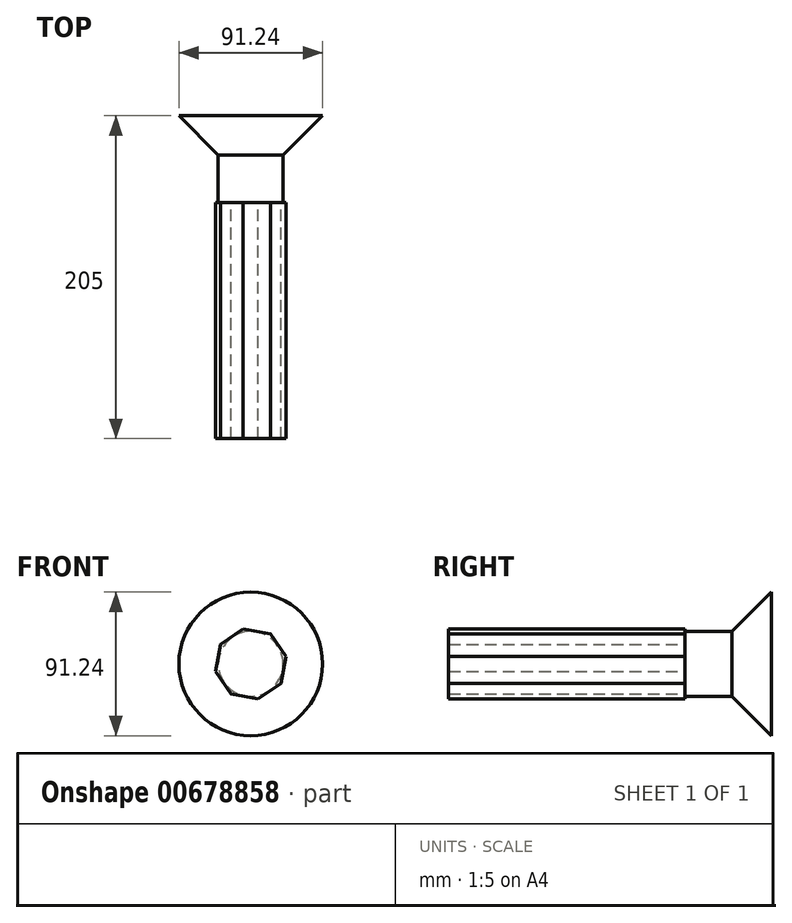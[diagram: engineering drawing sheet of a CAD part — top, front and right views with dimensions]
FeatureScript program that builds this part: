
annotation { "Feature Type Name" : "Feature", "Feature Type Description" : "" }
export const myFeature = defineFeature(function(context is Context, id is Id, definition is map)
    precondition{}
    {
        {
            var Q0;
            Q0=qCreatedBy(makeId("Front.planeOp"),FACE);
            var sketch = newSketch(context, id + "F0", { "sketchPlane" : qUnion([Q0])});
            skLineSegment(sketch, "E0.0", {"start": v(19.13, -12.45) * mm, "end": v(4.73, -22.33) * mm});
            skLineSegment(sketch, "E0.1", {"start": v(4.73, -22.33) * mm, "end": v(-12.45, -19.13) * mm});
            skLineSegment(sketch, "E0.2", {"start": v(-12.45, -19.13) * mm, "end": v(-22.33, -4.73) * mm});
            skLineSegment(sketch, "E0.3", {"start": v(-22.33, -4.73) * mm, "end": v(-19.13, 12.45) * mm});
            skLineSegment(sketch, "E0.4", {"start": v(-19.13, 12.45) * mm, "end": v(-4.73, 22.33) * mm});
            skLineSegment(sketch, "E0.5", {"start": v(-4.73, 22.33) * mm, "end": v(12.45, 19.13) * mm});
            skLineSegment(sketch, "E0.6", {"start": v(12.45, 19.13) * mm, "end": v(22.33, 4.73) * mm});
            skLineSegment(sketch, "E0.7", {"start": v(22.33, 4.73) * mm, "end": v(19.13, -12.45) * mm});
            skSolve(sketch);
        }
        {
            var Q0;
            Q0=makeQuery(id+"F0.imprint","IMPRINT",FACE,{"disambiguationData":[TD([[makeQuery(id+"F0.imprint","IMPRINT",EDGE,{"derivedFrom":sQuery(id+"F0.wireOp",EDGE,"E0.0")}),-1.0]])]});
            var Q1;
            Q1=sQuery(id+"F0.wireOp",EDGE,"E0.0");
            var Q2;
            Q2=sQuery(id+"F0.wireOp",EDGE,"E0.1");
            var Q3;
            Q3=sQuery(id+"F0.wireOp",EDGE,"E0.2");
            var Q4;
            Q4=sQuery(id+"F0.wireOp",EDGE,"E0.3");
            var Q5;
            Q5=sQuery(id+"F0.wireOp",EDGE,"E0.4");
            var Q6;
            Q6=sQuery(id+"F0.wireOp",EDGE,"E0.5");
            var Q7;
            Q7=sQuery(id+"F0.wireOp",EDGE,"E0.6");
            var Q8;
            Q8=sQuery(id+"F0.wireOp",EDGE,"E0.7");
            extrude(context, id + "F1", {"entities" : qUnion([Q0]), "surfaceEntities" : qUnion([Q1, Q2, Q3, Q4, Q5, Q6, Q7, Q8]), "depth" : 150 * mm, "offsetDistance" : 25 * mm});
        }
        {
            var Q0;
            Q0=makeQuery(id+"F1.opExtrude","CAP_FACE",FACE,{"disambiguationData":[OSD([sQuery(id+"F0.wireOp",EDGE,"E0.0"),sQuery(id+"F0.wireOp",EDGE,"E0.1"),sQuery(id+"F0.wireOp",EDGE,"E0.2"),sQuery(id+"F0.wireOp",EDGE,"E0.3"),sQuery(id+"F0.wireOp",EDGE,"E0.4"),sQuery(id+"F0.wireOp",EDGE,"E0.5"),sQuery(id+"F0.wireOp",EDGE,"E0.6"),sQuery(id+"F0.wireOp",EDGE,"E0.7")])],"isStart":true});
            var sketch = newSketch(context, id + "F2", { "sketchPlane" : qUnion([Q0])});
            skCircle(sketch, "E1", {"center": v(0, 0) * mm, "radius": 20.62 * mm});
            skSolve(sketch);
        }
        {
            var Q0;
            Q0=makeQuery(id+"F2.imprint","IMPRINT",FACE,{"disambiguationData":[TD([[makeQuery(id+"F2.imprint","IMPRINT",EDGE,{"derivedFrom":sQuery(id+"F2.wireOp",EDGE,"E1")}),1.0]])]});
            extrude(context, id + "F3", {"entities" : qUnion([Q0]), "operationType" : NewBodyOperationType.ADD, "depth" : 30 * mm, "offsetDistance" : 25 * mm});
        }
        {
            var Q0;
            Q0=makeQuery(id+"F3.opExtrude","CAP_FACE",FACE,{"disambiguationData":[OSD([sQuery(id+"F2.wireOp",EDGE,"E1")])],"isStart":false});
            extrude(context, id + "F4", {"entities" : qUnion([Q0]), "operationType" : NewBodyOperationType.ADD, "depth" : 25 * mm, "offsetDistance" : 25 * mm, "hasDraft" : true, "draftAngle" : 45 * degree});
        }
    });
